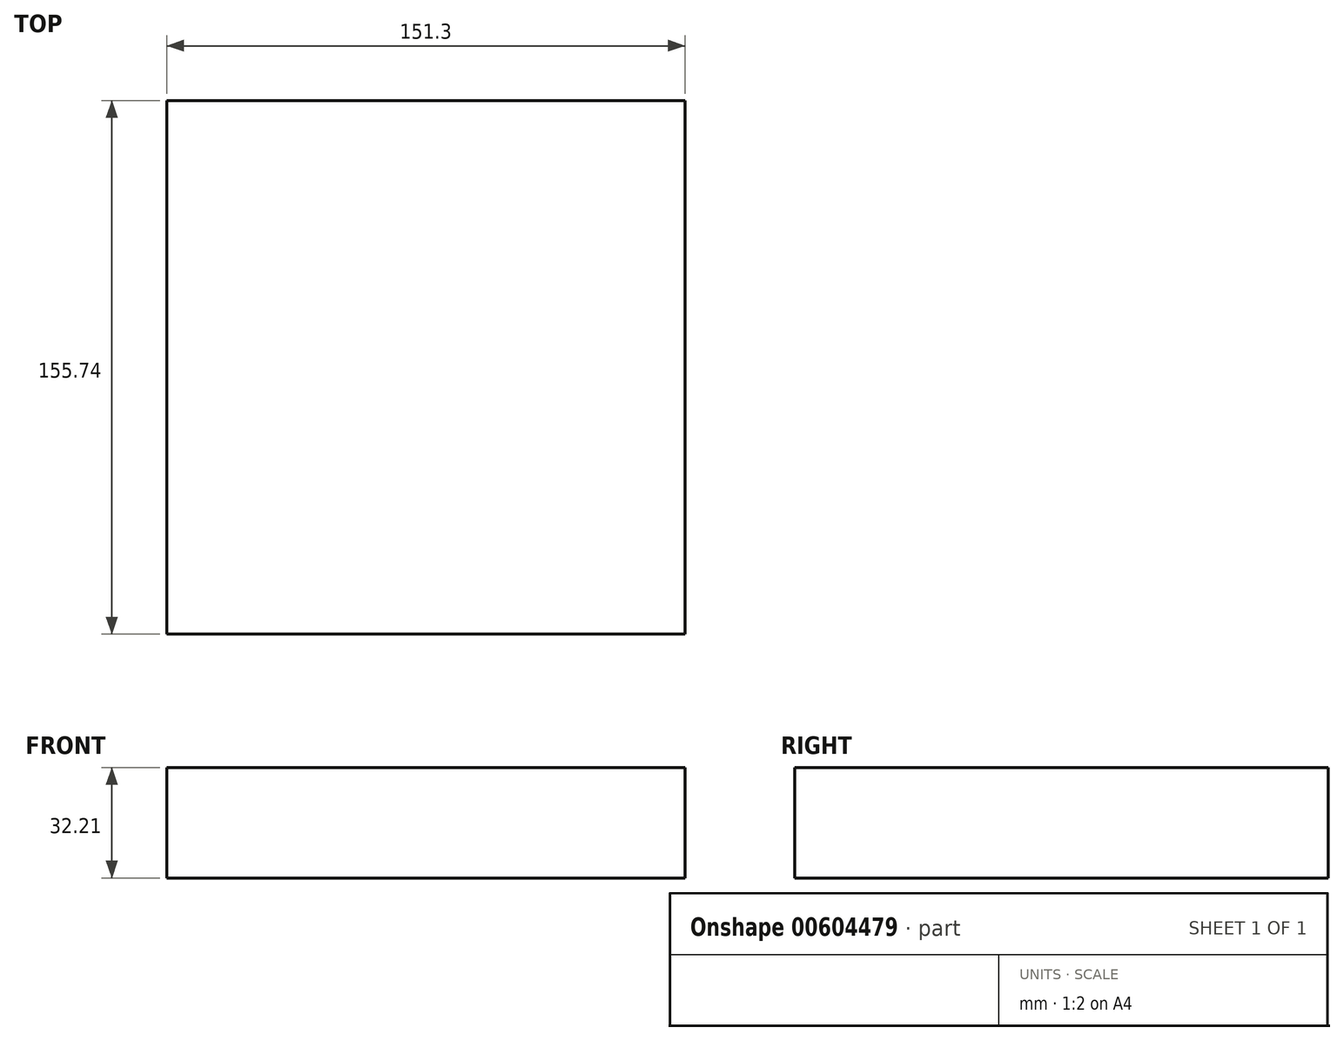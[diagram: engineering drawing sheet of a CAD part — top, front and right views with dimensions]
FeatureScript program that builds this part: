
annotation { "Feature Type Name" : "Feature", "Feature Type Description" : "" }
export const myFeature = defineFeature(function(context is Context, id is Id, definition is map)
    precondition{}
    {
        {
            var Q0;
            Q0=qCreatedBy(makeId("Top.planeOp"),FACE);
            var sketch = newSketch(context, id + "F0", { "sketchPlane" : qUnion([Q0])});
            skLineSegment(sketch, "E0.bottom", {"start": v(75.65, -77.87) * mm, "end": v(-75.65, -77.87) * mm});
            skLineSegment(sketch, "E0.top", {"start": v(75.65, 77.87) * mm, "end": v(-75.65, 77.87) * mm});
            skLineSegment(sketch, "E0.left", {"start": v(75.65, -77.87) * mm, "end": v(75.65, 77.87) * mm});
            skLineSegment(sketch, "E0.right", {"start": v(-75.65, -77.87) * mm, "end": v(-75.65, 77.87) * mm});
            skPoint(sketch, "E0.middle", {"position": v(0, 0) * mm});
            skSolve(sketch);
        }
        {
            var Q0;
            Q0=makeQuery(id+"F0.imprint","IMPRINT",FACE,{"disambiguationData":[TD([[makeQuery(id+"F0.imprint","IMPRINT",EDGE,{"derivedFrom":sQuery(id+"F0.wireOp",EDGE,"E0.bottom")}),-1.0]])]});
            var sketch = newSketch(context, id + "F1", { "sketchPlane" : qUnion([Q0])});
            skSolve(sketch);
        }
        {
            var Q0;
            Q0 = qSketchRegion(id + "F1", true);
            var Q1;
            Q1=makeQuery(id+"F0.imprint","IMPRINT",FACE,{"disambiguationData":[TD([[makeQuery(id+"F0.imprint","IMPRINT",EDGE,{"derivedFrom":sQuery(id+"F0.wireOp",EDGE,"E0.bottom")}),-1.0]])]});
            extrude(context, id + "F2", {"entities" : qUnion([Q0, Q1]), "depth" : 32.2 * mm, "offsetDistance" : 25.4 * mm});
        }
        {
            var Q0;
            Q0=makeQuery(id+"F2.opExtrude","CAP_FACE",FACE,{"disambiguationData":[OSD([sQuery(id+"F0.wireOp",EDGE,"E0.bottom"),sQuery(id+"F0.wireOp",EDGE,"E0.top"),sQuery(id+"F0.wireOp",EDGE,"E0.left"),sQuery(id+"F0.wireOp",EDGE,"E0.right")])],"isStart":false});
            var sketch = newSketch(context, id + "F3", { "sketchPlane" : qUnion([Q0])});
            skSolve(sketch);
        }
        {
            var Q0;
            Q0=makeQuery(id+"F3.imprint","IMPRINT",FACE,{"disambiguationData":[TD([[makeQuery(id+"F3.imprint","IMPRINT",EDGE,{"derivedFrom":makeQuery(id+"F2.opExtrude","CAP_EDGE",EDGE,{"disambiguationData":[OSD([sQuery(id+"F0.wireOp",EDGE,"E0.bottom")])],"isStart":false})}),-1.0]])]});
            var sketch = newSketch(context, id + "F4", { "sketchPlane" : qUnion([Q0])});
            skLineSegment(sketch, "E1.bottom", {"start": v(55.69, -62.08) * mm, "end": v(-55.69, -62.08) * mm});
            skLineSegment(sketch, "E1.top", {"start": v(55.69, 62.08) * mm, "end": v(-55.69, 62.08) * mm});
            skLineSegment(sketch, "E1.left", {"start": v(55.69, -62.08) * mm, "end": v(55.69, 62.08) * mm});
            skLineSegment(sketch, "E1.right", {"start": v(-55.69, -62.08) * mm, "end": v(-55.69, 62.08) * mm});
            skPoint(sketch, "E1.middle", {"position": v(0, 0) * mm});
            skSolve(sketch);
        }
        {
            var Q0;
            Q0=sQuery(id+"F4.wireOp",EDGE,"E1.top");
            var Q1;
            Q1=sQuery(id+"F4.wireOp",EDGE,"E1.right");
            var Q2;
            Q2=sQuery(id+"F4.wireOp",EDGE,"E1.bottom");
            var Q3;
            Q3=sQuery(id+"F4.wireOp",EDGE,"E1.left");
            extrude(context, id + "F5", {"bodyType" : ToolBodyType.SURFACE, "surfaceEntities" : qUnion([Q0, Q1, Q2, Q3]), "depth" : 20.3 * mm, "offsetDistance" : 30.48 * mm});
        }
    });
